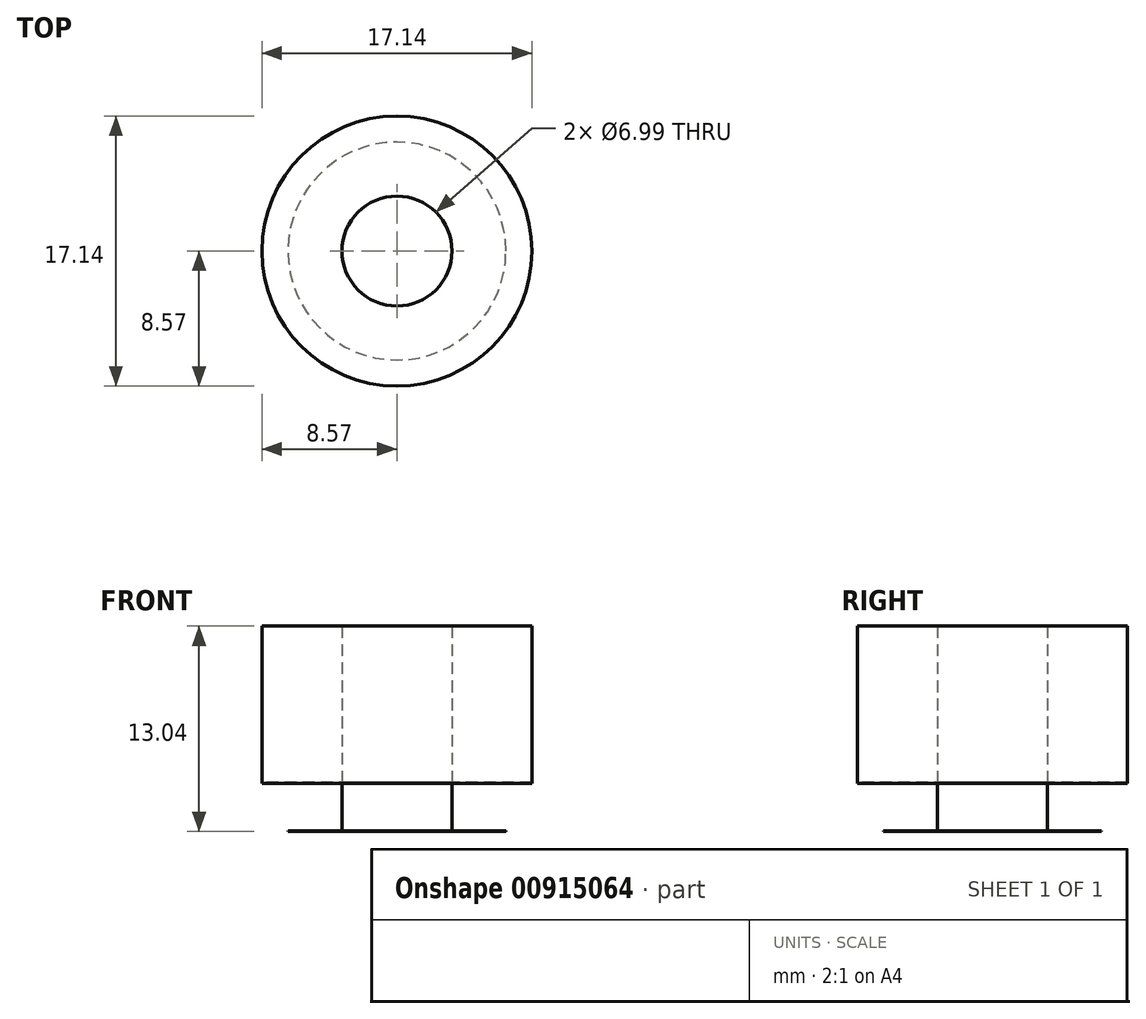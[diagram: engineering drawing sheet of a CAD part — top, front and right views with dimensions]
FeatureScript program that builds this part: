
annotation { "Feature Type Name" : "Feature", "Feature Type Description" : "" }
export const myFeature = defineFeature(function(context is Context, id is Id, definition is map)
    precondition{}
    {
        {
            var Q0;
            Q0=qCreatedBy(makeId("Top.planeOp"),FACE);
            var sketch = newSketch(context, id + "F0", { "sketchPlane" : qUnion([Q0])});
            skCircle(sketch, "E0", {"center": v(0, 0) * mm, "radius": 6.92 * mm});
            skSolve(sketch);
        }
        {
            var Q0;
            Q0 = qSketchRegion(id + "F0", true);
            extrude(context, id + "F1", {"entities" : qUnion([Q0]), "depth" : 0.04 * mm, "offsetDistance" : 25.4 * mm});
        }
        {
            var Q0;
            Q0=makeQuery(id+"F1.opExtrude","CAP_FACE",FACE,{"disambiguationData":[OSD([sQuery(id+"F0.wireOp",EDGE,"E0")])],"isStart":false});
            var sketch = newSketch(context, id + "F2", { "sketchPlane" : qUnion([Q0])});
            skCircle(sketch, "E1", {"center": v(0, 0) * mm, "radius": 3.5 * mm});
            skSolve(sketch);
        }
        {
            var Q0;
            Q0=makeQuery(id+"F2.imprint","IMPRINT",FACE,{"disambiguationData":[TD([[makeQuery(id+"F2.imprint","IMPRINT",EDGE,{"derivedFrom":sQuery(id+"F2.wireOp",EDGE,"E1")}),1.0]])]});
            extrude(context, id + "F3", {"entities" : qUnion([Q0]), "operationType" : NewBodyOperationType.ADD, "depth" : 3 * mm, "offsetDistance" : 25.4 * mm});
        }
        {
            var Q0;
            Q0=makeQuery(id+"F3.opExtrude","CAP_FACE",FACE,{"disambiguationData":[OSD([sQuery(id+"F2.wireOp",EDGE,"E1")])],"isStart":false});
            var sketch = newSketch(context, id + "F4", { "sketchPlane" : qUnion([Q0])});
            skCircle(sketch, "E2", {"center": v(0, 0) * mm, "radius": 8.57 * mm});
            skSolve(sketch);
        }
        {
            var Q0;
            Q0=makeQuery(id+"F4.imprint","IMPRINT",FACE,{"disambiguationData":[TD([[makeQuery(id+"F4.imprint","IMPRINT",EDGE,{"derivedFrom":sQuery(id+"F4.wireOp",EDGE,"E2")}),1.0]])]});
            extrude(context, id + "F5", {"entities" : qUnion([Q0]), "depth" : 10 * mm, "offsetDistance" : 25.4 * mm});
        }
        {
            var Q0;
            Q0=makeQuery(id+"F3.opExtrude","CAP_FACE",FACE,{"disambiguationData":[OSD([sQuery(id+"F2.wireOp",EDGE,"E1")])],"isStart":false});
            var sketch = newSketch(context, id + "F6", { "sketchPlane" : qUnion([Q0])});
            skSolve(sketch);
        }
        {
            var Q0;
            Q0=makeQuery(id+"F6.imprint","IMPRINT",FACE,{"disambiguationData":[TD([[makeQuery(id+"F6.imprint","IMPRINT",EDGE,{"derivedFrom":makeQuery(id+"F3.opExtrude","CAP_EDGE",EDGE,{"disambiguationData":[OSD([sQuery(id+"F2.wireOp",EDGE,"E1")])],"isStart":false})}),1.0]])]});
            var sketch = newSketch(context, id + "F7", { "sketchPlane" : qUnion([Q0])});
            skCircle(sketch, "E3", {"center": v(0, 0) * mm, "radius": 8.57 * mm});
            skSolve(sketch);
        }
        {
            var Q0;
            Q0=makeQuery(id+"F7.imprint","IMPRINT",FACE,{"disambiguationData":[TD([[makeQuery(id+"F7.imprint","IMPRINT",EDGE,{"derivedFrom":sQuery(id+"F7.wireOp",EDGE,"E3")}),1.0]])]});
            extrude(context, id + "F8", {"entities" : qUnion([Q0]), "depth" : 0.06 * mm, "offsetDistance" : 25.4 * mm});
        }
        {
            var Q0;
            Q0=makeQuery(id+"F6.imprint","IMPRINT",FACE,{"disambiguationData":[TD([[makeQuery(id+"F6.imprint","IMPRINT",EDGE,{"derivedFrom":makeQuery(id+"F3.opExtrude","CAP_EDGE",EDGE,{"disambiguationData":[OSD([sQuery(id+"F2.wireOp",EDGE,"E1")])],"isStart":false})}),1.0]])]});
            extrude(context, id + "F9", {"entities" : qUnion([Q0]), "depth" : 10 * mm, "offsetDistance" : 25.4 * mm});
        }
    });
